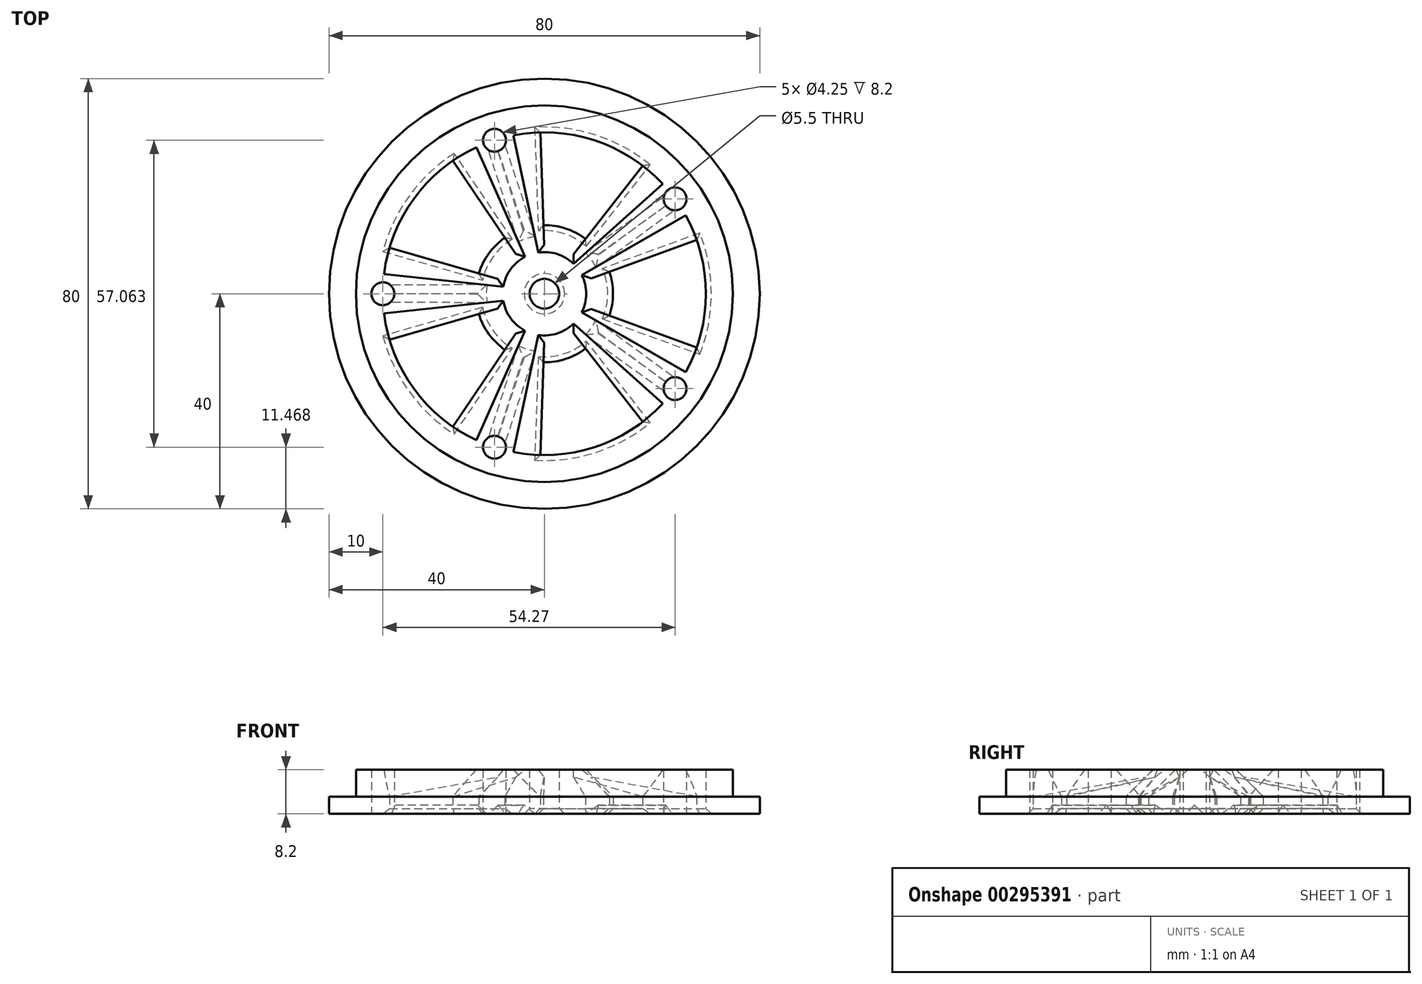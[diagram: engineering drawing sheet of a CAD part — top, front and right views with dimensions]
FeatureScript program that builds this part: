
annotation { "Feature Type Name" : "Feature", "Feature Type Description" : "" }
export const myFeature = defineFeature(function(context is Context, id is Id, definition is map)
    precondition{}
    {
        {
            var Q0;
            Q0=qCreatedBy(makeId("Top.planeOp"),FACE);
            var sketch = newSketch(context, id + "F0", { "sketchPlane" : qUnion([Q0])});
            skCircle(sketch, "E0", {"center": v(0, 0) * mm, "radius": 40 * mm});
            skCircle(sketch, "E1", {"center": v(0, 0) * mm, "radius": 2.75 * mm});
            skLineSegment(sketch, "E2", {"start": v(12.07, 4.1) * mm, "end": v(28.28, 10) * mm});
            skArc(sketch, "E3", {"start": v(12.07, 4.1) * mm, "mid": v(12.58, 2.08) * mm, "end": v(12.75, 0) * mm});
            skArc(sketch, "E4", {"start": v(28.28, 10) * mm, "mid": v(29.57, 5.07) * mm, "end": v(30, 0) * mm});
            skArc(sketch, "E5.MirrorCS", {"start": v(12.07, -4.1) * mm, "mid": v(12.58, -2.08) * mm, "end": v(12.75, 0) * mm});
            skLineSegment(sketch, "E6.MirrorCS", {"start": v(12.07, -4.1) * mm, "end": v(28.28, -10) * mm});
            skArc(sketch, "E7.MirrorCS", {"start": v(28.28, -10) * mm, "mid": v(29.57, -5.07) * mm, "end": v(30, 0) * mm});
            skArc(sketch, "E8.1.0", {"start": v(18.25, 23.8) * mm, "mid": v(13.96, 26.55) * mm, "end": v(9.27, 28.53) * mm});
            skLineSegment(sketch, "E8.1.1", {"start": v(-0.17, 12.75) * mm, "end": v(-0.77, 30) * mm});
            skLineSegment(sketch, "E8.1.2", {"start": v(7.63, 10.22) * mm, "end": v(18.25, 23.8) * mm});
            skArc(sketch, "E8.1.3", {"start": v(-0.77, 30) * mm, "mid": v(4.31, 29.69) * mm, "end": v(9.27, 28.53) * mm});
            skArc(sketch, "E8.1.4", {"start": v(7.63, 10.22) * mm, "mid": v(5.86, 11.32) * mm, "end": v(3.94, 12.13) * mm});
            skArc(sketch, "E8.1.5", {"start": v(-0.17, 12.75) * mm, "mid": v(1.91, 12.6) * mm, "end": v(3.94, 12.13) * mm});
            skArc(sketch, "E8.2.0", {"start": v(-17, 24.72) * mm, "mid": v(-20.94, 21.48) * mm, "end": v(-24.27, 17.63) * mm});
            skLineSegment(sketch, "E8.2.1", {"start": v(-12.18, 3.78) * mm, "end": v(-28.76, 8.53) * mm});
            skLineSegment(sketch, "E8.2.2", {"start": v(-7.36, 10.41) * mm, "end": v(-17, 24.72) * mm});
            skArc(sketch, "E8.2.3", {"start": v(-28.76, 8.53) * mm, "mid": v(-26.9, 13.28) * mm, "end": v(-24.27, 17.63) * mm});
            skArc(sketch, "E8.2.4", {"start": v(-7.36, 10.41) * mm, "mid": v(-8.96, 9.07) * mm, "end": v(-10.31, 7.5) * mm});
            skArc(sketch, "E8.2.5", {"start": v(-12.18, 3.78) * mm, "mid": v(-11.4, 5.71) * mm, "end": v(-10.31, 7.5) * mm});
            skArc(sketch, "E8.3.0", {"start": v(-28.76, -8.53) * mm, "mid": v(-26.9, -13.28) * mm, "end": v(-24.27, -17.63) * mm});
            skLineSegment(sketch, "E8.3.1", {"start": v(-7.36, -10.41) * mm, "end": v(-17, -24.72) * mm});
            skLineSegment(sketch, "E8.3.2", {"start": v(-12.18, -3.78) * mm, "end": v(-28.76, -8.53) * mm});
            skArc(sketch, "E8.3.3", {"start": v(-17, -24.72) * mm, "mid": v(-20.94, -21.48) * mm, "end": v(-24.27, -17.63) * mm});
            skArc(sketch, "E8.3.4", {"start": v(-12.18, -3.78) * mm, "mid": v(-11.4, -5.71) * mm, "end": v(-10.31, -7.5) * mm});
            skArc(sketch, "E8.3.5", {"start": v(-7.36, -10.41) * mm, "mid": v(-8.96, -9.07) * mm, "end": v(-10.31, -7.5) * mm});
            skArc(sketch, "E8.4.0", {"start": v(-0.77, -30) * mm, "mid": v(4.31, -29.69) * mm, "end": v(9.27, -28.53) * mm});
            skLineSegment(sketch, "E8.4.1", {"start": v(7.63, -10.22) * mm, "end": v(18.25, -23.8) * mm});
            skLineSegment(sketch, "E8.4.2", {"start": v(-0.17, -12.75) * mm, "end": v(-0.77, -30) * mm});
            skArc(sketch, "E8.4.3", {"start": v(18.25, -23.8) * mm, "mid": v(13.96, -26.55) * mm, "end": v(9.27, -28.53) * mm});
            skArc(sketch, "E8.4.4", {"start": v(-0.17, -12.75) * mm, "mid": v(1.91, -12.6) * mm, "end": v(3.94, -12.13) * mm});
            skArc(sketch, "E8.4.5", {"start": v(7.63, -10.22) * mm, "mid": v(5.86, -11.32) * mm, "end": v(3.94, -12.13) * mm});
            skSolve(sketch);
        }
        {
            var Q0;
            Q0 = qSketchRegion(id + "F0", true);
            extrude(context, id + "F1", {"entities" : qUnion([Q0]), "depth" : 3.2 * mm});
        }
        {
            var Q0;
            Q0=makeQuery(id+"F1.opExtrude","CAP_FACE",FACE,{"disambiguationData":[OSD([sQuery(id+"F0.wireOp",EDGE,"E0"),sQuery(id+"F0.wireOp",EDGE,"E1"),sQuery(id+"F0.wireOp",EDGE,"E2"),sQuery(id+"F0.wireOp",EDGE,"E3"),sQuery(id+"F0.wireOp",EDGE,"E4"),sQuery(id+"F0.wireOp",EDGE,"E5.MirrorCS"),sQuery(id+"F0.wireOp",EDGE,"E6.MirrorCS"),sQuery(id+"F0.wireOp",EDGE,"E7.MirrorCS"),sQuery(id+"F0.wireOp",EDGE,"E8.1.0"),sQuery(id+"F0.wireOp",EDGE,"E8.1.1"),sQuery(id+"F0.wireOp",EDGE,"E8.1.2"),sQuery(id+"F0.wireOp",EDGE,"E8.1.3"),sQuery(id+"F0.wireOp",EDGE,"E8.1.4"),sQuery(id+"F0.wireOp",EDGE,"E8.1.5"),sQuery(id+"F0.wireOp",EDGE,"E8.2.0"),sQuery(id+"F0.wireOp",EDGE,"E8.2.1"),sQuery(id+"F0.wireOp",EDGE,"E8.2.2"),sQuery(id+"F0.wireOp",EDGE,"E8.2.3"),sQuery(id+"F0.wireOp",EDGE,"E8.2.4"),sQuery(id+"F0.wireOp",EDGE,"E8.2.5"),sQuery(id+"F0.wireOp",EDGE,"E8.3.0"),sQuery(id+"F0.wireOp",EDGE,"E8.3.1"),sQuery(id+"F0.wireOp",EDGE,"E8.3.2"),sQuery(id+"F0.wireOp",EDGE,"E8.3.3"),sQuery(id+"F0.wireOp",EDGE,"E8.3.4"),sQuery(id+"F0.wireOp",EDGE,"E8.3.5"),sQuery(id+"F0.wireOp",EDGE,"E8.4.0"),sQuery(id+"F0.wireOp",EDGE,"E8.4.1"),sQuery(id+"F0.wireOp",EDGE,"E8.4.2"),sQuery(id+"F0.wireOp",EDGE,"E8.4.3"),sQuery(id+"F0.wireOp",EDGE,"E8.4.4"),sQuery(id+"F0.wireOp",EDGE,"E8.4.5")])],"isStart":false});
            var sketch = newSketch(context, id + "F2", { "sketchPlane" : qUnion([Q0])});
            skArc(sketch, "E9", {"start": v(21.96, 20.44) * mm, "mid": v(9.27, 28.53) * mm, "end": v(-5.75, 29.44) * mm});
            skCircle(sketch, "E10", {"center": v(0, 0) * mm, "radius": 35 * mm});
            skArc(sketch, "E11", {"start": v(5.42, 5.54) * mm, "mid": v(2.4, 7.37) * mm, "end": v(-1.13, 7.67) * mm});
            skCircle(sketch, "E12", {"center": v(0, 0) * mm, "radius": 2.75 * mm});
            skLineSegment(sketch, "E13", {"start": v(5.42, 5.54) * mm, "end": v(21.96, 20.44) * mm});
            skLineSegment(sketch, "E14", {"start": v(6.94, 3.44) * mm, "end": v(26.22, 14.57) * mm});
            skLineSegment(sketch, "E15.1.0", {"start": v(-3.6, 6.87) * mm, "end": v(-12.65, 27.2) * mm});
            skLineSegment(sketch, "E15.1.1", {"start": v(-1.13, 7.67) * mm, "end": v(-5.75, 29.44) * mm});
            skLineSegment(sketch, "E15.2.0", {"start": v(-7.64, -1.3) * mm, "end": v(-29.78, -3.63) * mm});
            skLineSegment(sketch, "E15.2.1", {"start": v(-7.64, 1.3) * mm, "end": v(-29.78, 3.63) * mm});
            skLineSegment(sketch, "E15.3.0", {"start": v(-1.13, -7.67) * mm, "end": v(-5.75, -29.44) * mm});
            skLineSegment(sketch, "E15.3.1", {"start": v(-3.6, -6.87) * mm, "end": v(-12.65, -27.2) * mm});
            skLineSegment(sketch, "E15.4.0", {"start": v(6.94, -3.44) * mm, "end": v(26.22, -14.57) * mm});
            skLineSegment(sketch, "E15.4.1", {"start": v(5.42, -5.54) * mm, "end": v(21.96, -20.44) * mm});
            skArc(sketch, "E16.trimOffspring", {"start": v(-3.6, 6.87) * mm, "mid": v(-6.27, 4.56) * mm, "end": v(-7.64, 1.3) * mm});
            skArc(sketch, "E17.trimOffspring", {"start": v(-7.64, -1.3) * mm, "mid": v(-6.27, -4.56) * mm, "end": v(-3.6, -6.87) * mm});
            skArc(sketch, "E18.trimOffspring", {"start": v(6.94, -3.44) * mm, "mid": v(7.75, 0) * mm, "end": v(6.94, 3.44) * mm});
            skArc(sketch, "E19.trimOffspring", {"start": v(-1.13, -7.67) * mm, "mid": v(2.4, -7.37) * mm, "end": v(5.42, -5.54) * mm});
            skArc(sketch, "E20.trimOffspring", {"start": v(26.22, -14.57) * mm, "mid": v(30, 0) * mm, "end": v(26.22, 14.57) * mm});
            skArc(sketch, "E21.trimOffspring", {"start": v(-12.65, 27.2) * mm, "mid": v(-24.27, 17.63) * mm, "end": v(-29.78, 3.63) * mm});
            skArc(sketch, "E22.trimOffspring", {"start": v(-29.78, -3.63) * mm, "mid": v(-24.27, -17.63) * mm, "end": v(-12.65, -27.2) * mm});
            skArc(sketch, "E23.trimOffspring", {"start": v(-5.75, -29.44) * mm, "mid": v(9.27, -28.53) * mm, "end": v(21.96, -20.44) * mm});
            skSolve(sketch);
        }
        {
            var Q0;
            Q0 = qSketchRegion(id + "F2", true);
            extrude(context, id + "F3", {"entities" : qUnion([Q0]), "operationType" : NewBodyOperationType.ADD, "depth" : 5 * mm});
        }
        {
            var Q0;
            Q0=makeQuery(id+"F3.opExtrude","CAP_EDGE",EDGE,{"disambiguationData":[OSD([sQuery(id+"F2.wireOp",EDGE,"E16.trimOffspring")])],"isStart":true});
            var Q1;
            Q1=makeQuery(id+"F3.opExtrude","CAP_EDGE",EDGE,{"disambiguationData":[OSD([sQuery(id+"F2.wireOp",EDGE,"E18.trimOffspring")])],"isStart":true});
            var Q2;
            Q2=makeQuery(id+"F3.opExtrude","CAP_EDGE",EDGE,{"disambiguationData":[OSD([sQuery(id+"F2.wireOp",EDGE,"E19.trimOffspring")])],"isStart":true});
            var Q3;
            Q3=makeQuery(id+"F3.opExtrude","CAP_EDGE",EDGE,{"disambiguationData":[OSD([sQuery(id+"F2.wireOp",EDGE,"E17.trimOffspring")])],"isStart":true});
            var Q4;
            Q4=makeQuery(id+"F3.opExtrude","CAP_EDGE",EDGE,{"disambiguationData":[OSD([sQuery(id+"F2.wireOp",EDGE,"E11")])],"isStart":true});
            chamfer(context, id + "F4", {"entities" : qUnion([Q0, Q1, Q2, Q3, Q4]), "width" : 5 * mm, "tangentPropagation" : true});
        }
        {
            var Q0;
            Q0=makeQuery(id+"F3.opExtrude","CAP_EDGE",EDGE,{"disambiguationData":[OSD([sQuery(id+"F2.wireOp",EDGE,"E15.2.0")])],"isStart":true});
            var Q1;
            Q1=makeQuery(id+"F3.opExtrude","CAP_EDGE",EDGE,{"disambiguationData":[OSD([sQuery(id+"F2.wireOp",EDGE,"E15.3.0")])],"isStart":true});
            var Q2;
            Q2=makeQuery(id+"F3.opExtrude","CAP_EDGE",EDGE,{"disambiguationData":[OSD([sQuery(id+"F2.wireOp",EDGE,"E15.4.1")])],"isStart":true});
            var Q3;
            Q3=makeQuery(id+"F3.opExtrude","CAP_EDGE",EDGE,{"disambiguationData":[OSD([sQuery(id+"F2.wireOp",EDGE,"E15.3.1")])],"isStart":true});
            var Q4;
            Q4=makeQuery(id+"F3.opExtrude","CAP_EDGE",EDGE,{"disambiguationData":[OSD([sQuery(id+"F2.wireOp",EDGE,"E15.2.1")])],"isStart":true});
            var Q5;
            Q5=makeQuery(id+"F3.opExtrude","CAP_EDGE",EDGE,{"disambiguationData":[OSD([sQuery(id+"F2.wireOp",EDGE,"E15.4.0")])],"isStart":true});
            var Q6;
            Q6=makeQuery(id+"F3.opExtrude","CAP_EDGE",EDGE,{"disambiguationData":[OSD([sQuery(id+"F2.wireOp",EDGE,"E14")])],"isStart":true});
            var Q7;
            Q7=makeQuery(id+"F3.opExtrude","CAP_EDGE",EDGE,{"disambiguationData":[OSD([sQuery(id+"F2.wireOp",EDGE,"E13")])],"isStart":true});
            var Q8;
            Q8=makeQuery(id+"F3.opExtrude","CAP_EDGE",EDGE,{"disambiguationData":[OSD([sQuery(id+"F2.wireOp",EDGE,"E15.1.1")])],"isStart":true});
            var Q9;
            Q9=makeQuery(id+"F3.opExtrude","CAP_EDGE",EDGE,{"disambiguationData":[OSD([sQuery(id+"F2.wireOp",EDGE,"E15.1.0")])],"isStart":true});
            chamfer(context, id + "F5", {"entities" : qUnion([Q0, Q1, Q2, Q3, Q4, Q5, Q6, Q7, Q8, Q9]), "width" : 5 * mm, "tangentPropagation" : true});
        }
        {
            var Q0;
            Q0=qCreatedBy(makeId("Top.planeOp"),FACE);
            var sketch = newSketch(context, id + "F6", { "sketchPlane" : qUnion([Q0])});
            skCircle(sketch, "E24", {"center": v(24.27, 17.63) * mm, "radius": 2.12 * mm});
            skLineSegment(sketch, "E25", {"start": v(0, 0) * mm, "end": v(28.32, 20.57) * mm, "construction": true});
            skCircle(sketch, "E26.1.0", {"center": v(-9.27, 28.53) * mm, "radius": 2.12 * mm});
            skCircle(sketch, "E26.2.0", {"center": v(-30, 0) * mm, "radius": 2.12 * mm});
            skCircle(sketch, "E26.3.0", {"center": v(-9.27, -28.53) * mm, "radius": 2.12 * mm});
            skCircle(sketch, "E26.4.0", {"center": v(24.27, -17.63) * mm, "radius": 2.12 * mm});
            skPoint(sketch, "E26.center", {"position": v(0, 0) * mm});
            skSolve(sketch);
        }
        {
            var Q0;
            Q0 = qSketchRegion(id + "F6", true);
            extrude(context, id + "F7", {"entities" : qUnion([Q0]), "operationType" : NewBodyOperationType.REMOVE, "depth" : 25 * mm});
        }
        {
            var Q0;
            Q0=makeQuery(id+"F1.opExtrude","CAP_FACE",FACE,{"disambiguationData":[OSD([sQuery(id+"F0.wireOp",EDGE,"E0"),sQuery(id+"F0.wireOp",EDGE,"E1"),sQuery(id+"F0.wireOp",EDGE,"E2"),sQuery(id+"F0.wireOp",EDGE,"E3"),sQuery(id+"F0.wireOp",EDGE,"E4"),sQuery(id+"F0.wireOp",EDGE,"E5.MirrorCS"),sQuery(id+"F0.wireOp",EDGE,"E6.MirrorCS"),sQuery(id+"F0.wireOp",EDGE,"E7.MirrorCS"),sQuery(id+"F0.wireOp",EDGE,"E8.1.0"),sQuery(id+"F0.wireOp",EDGE,"E8.1.1"),sQuery(id+"F0.wireOp",EDGE,"E8.1.2"),sQuery(id+"F0.wireOp",EDGE,"E8.1.3"),sQuery(id+"F0.wireOp",EDGE,"E8.1.4"),sQuery(id+"F0.wireOp",EDGE,"E8.1.5"),sQuery(id+"F0.wireOp",EDGE,"E8.2.0"),sQuery(id+"F0.wireOp",EDGE,"E8.2.1"),sQuery(id+"F0.wireOp",EDGE,"E8.2.2"),sQuery(id+"F0.wireOp",EDGE,"E8.2.3"),sQuery(id+"F0.wireOp",EDGE,"E8.2.4"),sQuery(id+"F0.wireOp",EDGE,"E8.2.5"),sQuery(id+"F0.wireOp",EDGE,"E8.3.0"),sQuery(id+"F0.wireOp",EDGE,"E8.3.1"),sQuery(id+"F0.wireOp",EDGE,"E8.3.2"),sQuery(id+"F0.wireOp",EDGE,"E8.3.3"),sQuery(id+"F0.wireOp",EDGE,"E8.3.4"),sQuery(id+"F0.wireOp",EDGE,"E8.3.5"),sQuery(id+"F0.wireOp",EDGE,"E8.4.0"),sQuery(id+"F0.wireOp",EDGE,"E8.4.1"),sQuery(id+"F0.wireOp",EDGE,"E8.4.2"),sQuery(id+"F0.wireOp",EDGE,"E8.4.3"),sQuery(id+"F0.wireOp",EDGE,"E8.4.4"),sQuery(id+"F0.wireOp",EDGE,"E8.4.5")])],"isStart":true});
            var sketch = newSketch(context, id + "F8", { "sketchPlane" : qUnion([Q0])});
            skLineSegment(sketch, "E27", {"start": v(23.03, 19.36) * mm, "end": v(6.8, 7.67) * mm});
            skLineSegment(sketch, "E28", {"start": v(25.53, 15.92) * mm, "end": v(9.4, 4.1) * mm});
            skArc(sketch, "E29", {"start": v(6.8, 7.67) * mm, "mid": v(8.3, 6.02) * mm, "end": v(9.4, 4.1) * mm});
            skArc(sketch, "E30", {"start": v(23.03, 19.36) * mm, "mid": v(25.99, 18.88) * mm, "end": v(25.53, 15.92) * mm});
            skLineSegment(sketch, "E31.1.0", {"start": v(-11.3, 27.88) * mm, "end": v(-5.2, 8.84) * mm});
            skArc(sketch, "E31.1.1", {"start": v(-11.3, 27.88) * mm, "mid": v(-9.93, 30.55) * mm, "end": v(-7.25, 29.2) * mm});
            skLineSegment(sketch, "E31.1.2", {"start": v(-7.25, 29.2) * mm, "end": v(-1, 10.2) * mm});
            skArc(sketch, "E31.1.3", {"start": v(-5.2, 8.84) * mm, "mid": v(-3.17, 9.75) * mm, "end": v(-1, 10.2) * mm});
            skLineSegment(sketch, "E31.2.0", {"start": v(-30, -2.12) * mm, "end": v(-10, -2.2) * mm});
            skArc(sketch, "E31.2.1", {"start": v(-30, -2.12) * mm, "mid": v(-32.12, 0) * mm, "end": v(-30, 2.12) * mm});
            skLineSegment(sketch, "E31.2.2", {"start": v(-30, 2.12) * mm, "end": v(-10, 2.2) * mm});
            skArc(sketch, "E31.2.3", {"start": v(-10, -2.2) * mm, "mid": v(-10.25, 0) * mm, "end": v(-10, 2.2) * mm});
            skLineSegment(sketch, "E31.3.0", {"start": v(-7.25, -29.2) * mm, "end": v(-1, -10.2) * mm});
            skArc(sketch, "E31.3.1", {"start": v(-7.25, -29.2) * mm, "mid": v(-9.93, -30.55) * mm, "end": v(-11.3, -27.88) * mm});
            skLineSegment(sketch, "E31.3.2", {"start": v(-11.3, -27.88) * mm, "end": v(-5.2, -8.84) * mm});
            skArc(sketch, "E31.3.3", {"start": v(-1, -10.2) * mm, "mid": v(-3.17, -9.75) * mm, "end": v(-5.2, -8.84) * mm});
            skLineSegment(sketch, "E31.4.0", {"start": v(25.53, -15.92) * mm, "end": v(9.4, -4.1) * mm});
            skArc(sketch, "E31.4.1", {"start": v(25.53, -15.92) * mm, "mid": v(25.99, -18.88) * mm, "end": v(23.03, -19.36) * mm});
            skLineSegment(sketch, "E31.4.2", {"start": v(23.03, -19.36) * mm, "end": v(6.8, -7.67) * mm});
            skArc(sketch, "E31.4.3", {"start": v(9.4, -4.1) * mm, "mid": v(8.3, -6.02) * mm, "end": v(6.8, -7.67) * mm});
            skSolve(sketch);
        }
        {
            var Q0;
            Q0 = qSketchRegion(id + "F8", true);
            extrude(context, id + "F9", {"entities" : qUnion([Q0]), "operationType" : NewBodyOperationType.REMOVE, "oppositeDirection" : true, "depth" : 1.6 * mm});
        }
        {
            var Q0;
            Q0=makeQuery(id+"F9.boolean.opBoolean","COPY",EDGE,{"derivedFrom":makeQuery(id+"F9.opExtrude","CAP_EDGE",EDGE,{"disambiguationData":[OSD([sQuery(id+"F8.wireOp",EDGE,"E31.2.2")])],"isStart":false})});
            var Q1;
            Q1=makeQuery(id+"F9.boolean.opBoolean","COPY",EDGE,{"derivedFrom":makeQuery(id+"F9.opExtrude","CAP_EDGE",EDGE,{"disambiguationData":[OSD([sQuery(id+"F8.wireOp",EDGE,"E31.2.0")])],"isStart":false})});
            var Q2;
            Q2=makeQuery(id+"F9.boolean.opBoolean","COPY",EDGE,{"derivedFrom":makeQuery(id+"F9.opExtrude","CAP_EDGE",EDGE,{"disambiguationData":[OSD([sQuery(id+"F8.wireOp",EDGE,"E31.2.3")])],"isStart":false})});
            var Q3;
            Q3=makeQuery(id+"F9.boolean.opBoolean","COPY",EDGE,{"derivedFrom":makeQuery(id+"F9.opExtrude","CAP_EDGE",EDGE,{"disambiguationData":[OSD([sQuery(id+"F8.wireOp",EDGE,"E31.1.0")])],"isStart":false})});
            var Q4;
            Q4=makeQuery(id+"F9.boolean.opBoolean","COPY",EDGE,{"derivedFrom":makeQuery(id+"F9.opExtrude","CAP_EDGE",EDGE,{"disambiguationData":[OSD([sQuery(id+"F8.wireOp",EDGE,"E31.1.3")])],"isStart":false})});
            var Q5;
            Q5=makeQuery(id+"F9.boolean.opBoolean","COPY",EDGE,{"derivedFrom":makeQuery(id+"F9.opExtrude","CAP_EDGE",EDGE,{"disambiguationData":[OSD([sQuery(id+"F8.wireOp",EDGE,"E31.1.2")])],"isStart":false})});
            var Q6;
            Q6=makeQuery(id+"F9.boolean.opBoolean","COPY",EDGE,{"derivedFrom":makeQuery(id+"F9.opExtrude","CAP_EDGE",EDGE,{"disambiguationData":[OSD([sQuery(id+"F8.wireOp",EDGE,"E27")])],"isStart":false})});
            var Q7;
            Q7=makeQuery(id+"F9.boolean.opBoolean","COPY",EDGE,{"derivedFrom":makeQuery(id+"F9.opExtrude","CAP_EDGE",EDGE,{"disambiguationData":[OSD([sQuery(id+"F8.wireOp",EDGE,"E29")])],"isStart":false})});
            var Q8;
            Q8=makeQuery(id+"F9.boolean.opBoolean","COPY",EDGE,{"derivedFrom":makeQuery(id+"F9.opExtrude","CAP_EDGE",EDGE,{"disambiguationData":[OSD([sQuery(id+"F8.wireOp",EDGE,"E28")])],"isStart":false})});
            var Q9;
            Q9=makeQuery(id+"F9.boolean.opBoolean","COPY",EDGE,{"derivedFrom":makeQuery(id+"F9.opExtrude","CAP_EDGE",EDGE,{"disambiguationData":[OSD([sQuery(id+"F8.wireOp",EDGE,"E31.4.2")])],"isStart":false})});
            var Q10;
            Q10=makeQuery(id+"F9.boolean.opBoolean","COPY",EDGE,{"derivedFrom":makeQuery(id+"F9.opExtrude","CAP_EDGE",EDGE,{"disambiguationData":[OSD([sQuery(id+"F8.wireOp",EDGE,"E31.4.3")])],"isStart":false})});
            var Q11;
            Q11=makeQuery(id+"F9.boolean.opBoolean","COPY",EDGE,{"derivedFrom":makeQuery(id+"F9.opExtrude","CAP_EDGE",EDGE,{"disambiguationData":[OSD([sQuery(id+"F8.wireOp",EDGE,"E31.4.0")])],"isStart":false})});
            var Q12;
            Q12=makeQuery(id+"F9.boolean.opBoolean","COPY",EDGE,{"derivedFrom":makeQuery(id+"F9.opExtrude","CAP_EDGE",EDGE,{"disambiguationData":[OSD([sQuery(id+"F8.wireOp",EDGE,"E31.3.3")])],"isStart":false})});
            var Q13;
            Q13=makeQuery(id+"F9.boolean.opBoolean","COPY",EDGE,{"derivedFrom":makeQuery(id+"F9.opExtrude","CAP_EDGE",EDGE,{"disambiguationData":[OSD([sQuery(id+"F8.wireOp",EDGE,"E31.3.0")])],"isStart":false})});
            var Q14;
            Q14=makeQuery(id+"F9.boolean.opBoolean","COPY",EDGE,{"derivedFrom":makeQuery(id+"F9.opExtrude","CAP_EDGE",EDGE,{"disambiguationData":[OSD([sQuery(id+"F8.wireOp",EDGE,"E31.3.2")])],"isStart":false})});
            chamfer(context, id + "F10", {"entities" : qUnion([Q0, Q1, Q2, Q3, Q4, Q5, Q6, Q7, Q8, Q9, Q10, Q11, Q12, Q13, Q14]), "width" : 2.12 * mm, "tangentPropagation" : true});
        }
        {
            var Q0;
            Q0=makeQuery(id+"F1.opExtrude","CAP_EDGE",EDGE,{"disambiguationData":[OSD([sQuery(id+"F0.wireOp",EDGE,"E8.3.2")])],"isStart":true});
            var Q1;
            Q1=makeQuery(id+"F1.opExtrude","CAP_EDGE",EDGE,{"disambiguationData":[OSD([sQuery(id+"F0.wireOp",EDGE,"E8.3.4"),sQuery(id+"F0.wireOp",EDGE,"E8.3.5")])],"isStart":true});
            var Q2;
            Q2=makeQuery(id+"F1.opExtrude","CAP_EDGE",EDGE,{"disambiguationData":[OSD([sQuery(id+"F0.wireOp",EDGE,"E8.3.1")])],"isStart":true});
            var Q3;
            Q3=makeQuery(id+"F1.opExtrude","CAP_EDGE",EDGE,{"disambiguationData":[OSD([sQuery(id+"F0.wireOp",EDGE,"E8.3.0"),sQuery(id+"F0.wireOp",EDGE,"E8.3.3")])],"isStart":true});
            var Q4;
            Q4=makeQuery(id+"F1.opExtrude","CAP_EDGE",EDGE,{"disambiguationData":[OSD([sQuery(id+"F0.wireOp",EDGE,"E8.4.2")])],"isStart":true});
            var Q5;
            Q5=makeQuery(id+"F1.opExtrude","CAP_EDGE",EDGE,{"disambiguationData":[OSD([sQuery(id+"F0.wireOp",EDGE,"E8.4.0"),sQuery(id+"F0.wireOp",EDGE,"E8.4.3")])],"isStart":true});
            var Q6;
            Q6=makeQuery(id+"F1.opExtrude","CAP_EDGE",EDGE,{"disambiguationData":[OSD([sQuery(id+"F0.wireOp",EDGE,"E8.4.1")])],"isStart":true});
            var Q7;
            Q7=makeQuery(id+"F1.opExtrude","CAP_EDGE",EDGE,{"disambiguationData":[OSD([sQuery(id+"F0.wireOp",EDGE,"E8.4.4"),sQuery(id+"F0.wireOp",EDGE,"E8.4.5")])],"isStart":true});
            var Q8;
            Q8=makeQuery(id+"F1.opExtrude","CAP_EDGE",EDGE,{"disambiguationData":[OSD([sQuery(id+"F0.wireOp",EDGE,"E6.MirrorCS")])],"isStart":true});
            var Q9;
            Q9=makeQuery(id+"F1.opExtrude","CAP_EDGE",EDGE,{"disambiguationData":[OSD([sQuery(id+"F0.wireOp",EDGE,"E3"),sQuery(id+"F0.wireOp",EDGE,"E5.MirrorCS")])],"isStart":true});
            var Q10;
            Q10=makeQuery(id+"F1.opExtrude","CAP_EDGE",EDGE,{"disambiguationData":[OSD([sQuery(id+"F0.wireOp",EDGE,"E2")])],"isStart":true});
            var Q11;
            Q11=makeQuery(id+"F1.opExtrude","CAP_EDGE",EDGE,{"disambiguationData":[OSD([sQuery(id+"F0.wireOp",EDGE,"E4"),sQuery(id+"F0.wireOp",EDGE,"E7.MirrorCS")])],"isStart":true});
            var Q12;
            Q12=makeQuery(id+"F1.opExtrude","CAP_EDGE",EDGE,{"disambiguationData":[OSD([sQuery(id+"F0.wireOp",EDGE,"E8.1.0"),sQuery(id+"F0.wireOp",EDGE,"E8.1.3")])],"isStart":true});
            var Q13;
            Q13=makeQuery(id+"F1.opExtrude","CAP_EDGE",EDGE,{"disambiguationData":[OSD([sQuery(id+"F0.wireOp",EDGE,"E8.1.2")])],"isStart":true});
            var Q14;
            Q14=makeQuery(id+"F1.opExtrude","CAP_EDGE",EDGE,{"disambiguationData":[OSD([sQuery(id+"F0.wireOp",EDGE,"E8.1.1")])],"isStart":true});
            var Q15;
            Q15=makeQuery(id+"F1.opExtrude","CAP_EDGE",EDGE,{"disambiguationData":[OSD([sQuery(id+"F0.wireOp",EDGE,"E8.1.4"),sQuery(id+"F0.wireOp",EDGE,"E8.1.5")])],"isStart":true});
            var Q16;
            Q16=makeQuery(id+"F1.opExtrude","CAP_EDGE",EDGE,{"disambiguationData":[OSD([sQuery(id+"F0.wireOp",EDGE,"E8.2.2")])],"isStart":true});
            var Q17;
            Q17=makeQuery(id+"F1.opExtrude","CAP_EDGE",EDGE,{"disambiguationData":[OSD([sQuery(id+"F0.wireOp",EDGE,"E8.2.0"),sQuery(id+"F0.wireOp",EDGE,"E8.2.3")])],"isStart":true});
            var Q18;
            Q18=makeQuery(id+"F1.opExtrude","CAP_EDGE",EDGE,{"disambiguationData":[OSD([sQuery(id+"F0.wireOp",EDGE,"E8.2.1")])],"isStart":true});
            var Q19;
            Q19=makeQuery(id+"F1.opExtrude","CAP_EDGE",EDGE,{"disambiguationData":[OSD([sQuery(id+"F0.wireOp",EDGE,"E8.2.4"),sQuery(id+"F0.wireOp",EDGE,"E8.2.5")])],"isStart":true});
            var Q20;
            Q20=makeQuery(id+"F1.opExtrude","CAP_EDGE",EDGE,{"disambiguationData":[OSD([sQuery(id+"F0.wireOp",EDGE,"E1")])],"isStart":true});
            chamfer(context, id + "F11", {"entities" : qUnion([Q0, Q1, Q2, Q3, Q4, Q5, Q6, Q7, Q8, Q9, Q10, Q11, Q12, Q13, Q14, Q15, Q16, Q17, Q18, Q19, Q20]), "width" : 1 * mm, "tangentPropagation" : true});
        }
    });
